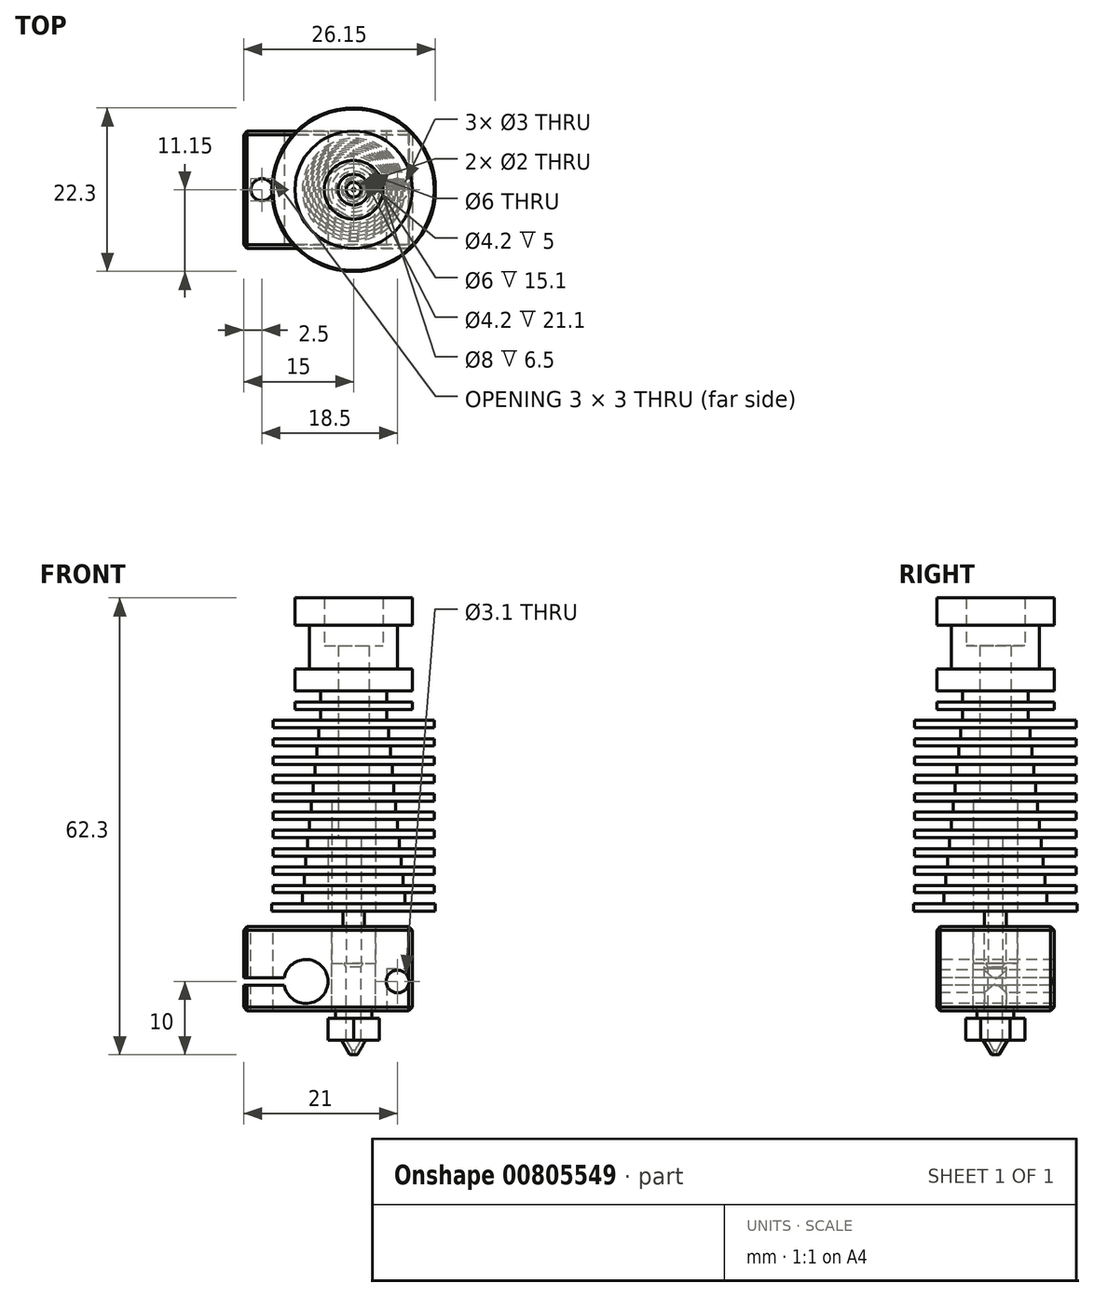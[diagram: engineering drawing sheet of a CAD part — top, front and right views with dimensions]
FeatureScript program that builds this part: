
annotation { "Feature Type Name" : "Feature", "Feature Type Description" : "" }
export const myFeature = defineFeature(function(context is Context, id is Id, definition is map)
    precondition{}
    {
        {
            var Q0;
            Q0=qCreatedBy(makeId("Front.planeOp"),FACE);
            var sketch = newSketch(context, id + "F0", { "sketchPlane" : qUnion([Q0])});
            skLineSegment(sketch, "E0", {"start": v(0, 0) * mm, "end": v(0, 45.21) * mm, "construction": true});
            skLineSegment(sketch, "E1", {"start": v(-3, 0) * mm, "end": v(-3, 15.1) * mm});
            skLineSegment(sketch, "E2", {"start": v(-3, 15.1) * mm, "end": v(-2.1, 15.1) * mm});
            skLineSegment(sketch, "E3", {"start": v(-2.1, 36.2) * mm, "end": v(-4, 36.2) * mm});
            skLineSegment(sketch, "E4", {"start": v(-4, 36.2) * mm, "end": v(-4, 42.7) * mm});
            skLineSegment(sketch, "E5", {"start": v(-4, 42.7) * mm, "end": v(-8, 42.7) * mm});
            skLineSegment(sketch, "E6", {"start": v(-8, 42.7) * mm, "end": v(-8, 39) * mm});
            skLineSegment(sketch, "E7", {"start": v(-6, 39) * mm, "end": v(-6, 33) * mm});
            skLineSegment(sketch, "E8", {"start": v(-6, 33) * mm, "end": v(-8, 33) * mm});
            skLineSegment(sketch, "E9", {"start": v(-8, 33) * mm, "end": v(-8, 30) * mm});
            skLineSegment(sketch, "E10", {"start": v(-8, 30) * mm, "end": v(-4.5, 30) * mm});
            skLineSegment(sketch, "E11", {"start": v(-4.5, 28.5) * mm, "end": v(-8, 28.5) * mm});
            skLineSegment(sketch, "E12", {"start": v(-8, 28.5) * mm, "end": v(-8, 27.5) * mm});
            skLineSegment(sketch, "E13", {"start": v(-8, 27.5) * mm, "end": v(-4.5, 27.5) * mm});
            skLineSegment(sketch, "E14", {"start": v(-4.5, 30) * mm, "end": v(-4.5, 28.5) * mm});
            skLineSegment(sketch, "E15", {"start": v(-8, 39) * mm, "end": v(-6, 39) * mm});
            skLineSegment(sketch, "E16", {"start": v(-2.1, 15.1) * mm, "end": v(-2.1, 36.2) * mm});
            skLineSegment(sketch, "E17", {"start": v(-11.15, 1) * mm, "end": v(-7, 1) * mm});
            skLineSegment(sketch, "E18", {"start": v(-7, 1) * mm, "end": v(-7, 2.5) * mm});
            skLineSegment(sketch, "E19", {"start": v(-7, 2.5) * mm, "end": v(-11, 2.5) * mm});
            skLineSegment(sketch, "E20", {"start": v(-11, 2.5) * mm, "end": v(-11, 3.5) * mm});
            skLineSegment(sketch, "E21", {"start": v(-11, 3.5) * mm, "end": v(-6.75, 3.5) * mm});
            skLineSegment(sketch, "E22", {"start": v(-6.75, 3.5) * mm, "end": v(-6.75, 5) * mm});
            skLineSegment(sketch, "E23", {"start": v(-6.75, 5) * mm, "end": v(-11, 5) * mm});
            skLineSegment(sketch, "E24", {"start": v(-11, 5) * mm, "end": v(-11, 6) * mm});
            skLineSegment(sketch, "E25", {"start": v(-11, 6) * mm, "end": v(-6.5, 6) * mm});
            skLineSegment(sketch, "E26", {"start": v(-6.5, 6) * mm, "end": v(-6.5, 7.5) * mm});
            skLineSegment(sketch, "E27", {"start": v(-6.5, 7.5) * mm, "end": v(-11, 7.5) * mm});
            skLineSegment(sketch, "E28", {"start": v(-11, 7.5) * mm, "end": v(-11, 8.5) * mm});
            skLineSegment(sketch, "E29", {"start": v(-11, 8.5) * mm, "end": v(-6.25, 8.5) * mm});
            skLineSegment(sketch, "E30", {"start": v(-6.25, 8.5) * mm, "end": v(-6.25, 10) * mm});
            skLineSegment(sketch, "E31", {"start": v(-6.25, 10) * mm, "end": v(-11, 10) * mm});
            skLineSegment(sketch, "E32", {"start": v(-11, 10) * mm, "end": v(-11, 11) * mm});
            skLineSegment(sketch, "E33", {"start": v(-11, 11) * mm, "end": v(-6, 11) * mm});
            skLineSegment(sketch, "E34", {"start": v(-6, 11) * mm, "end": v(-6, 12.5) * mm});
            skLineSegment(sketch, "E35", {"start": v(-6, 12.5) * mm, "end": v(-11, 12.5) * mm});
            skLineSegment(sketch, "E36", {"start": v(-11, 12.5) * mm, "end": v(-11, 13.5) * mm});
            skLineSegment(sketch, "E37", {"start": v(-11, 13.5) * mm, "end": v(-5.75, 13.5) * mm});
            skLineSegment(sketch, "E38", {"start": v(-5.75, 13.5) * mm, "end": v(-5.75, 15) * mm});
            skLineSegment(sketch, "E39", {"start": v(-5.75, 15) * mm, "end": v(-11, 15) * mm});
            skLineSegment(sketch, "E40", {"start": v(-11, 15) * mm, "end": v(-11, 16) * mm});
            skLineSegment(sketch, "E41", {"start": v(-11, 16) * mm, "end": v(-5.5, 16) * mm});
            skLineSegment(sketch, "E42", {"start": v(-5.5, 16) * mm, "end": v(-5.5, 17.5) * mm});
            skLineSegment(sketch, "E43", {"start": v(-5.5, 17.5) * mm, "end": v(-11, 17.5) * mm});
            skLineSegment(sketch, "E44", {"start": v(-11, 17.5) * mm, "end": v(-11, 18.5) * mm});
            skLineSegment(sketch, "E45", {"start": v(-11, 18.5) * mm, "end": v(-5.25, 18.5) * mm});
            skLineSegment(sketch, "E46", {"start": v(-5.25, 18.5) * mm, "end": v(-5.25, 20) * mm});
            skLineSegment(sketch, "E47", {"start": v(-5.25, 20) * mm, "end": v(-11, 20) * mm});
            skLineSegment(sketch, "E48", {"start": v(-11, 20) * mm, "end": v(-11, 21) * mm});
            skLineSegment(sketch, "E49", {"start": v(-11, 21) * mm, "end": v(-5, 21) * mm});
            skLineSegment(sketch, "E50", {"start": v(-5, 21) * mm, "end": v(-5, 22.5) * mm});
            skLineSegment(sketch, "E51", {"start": v(-5, 22.5) * mm, "end": v(-11, 22.5) * mm});
            skLineSegment(sketch, "E52", {"start": v(-11, 22.5) * mm, "end": v(-11, 23.5) * mm});
            skLineSegment(sketch, "E53", {"start": v(-11, 23.5) * mm, "end": v(-4.75, 23.5) * mm});
            skLineSegment(sketch, "E54", {"start": v(-4.75, 23.5) * mm, "end": v(-4.75, 25) * mm});
            skLineSegment(sketch, "E55", {"start": v(-4.75, 25) * mm, "end": v(-11, 25) * mm});
            skLineSegment(sketch, "E56", {"start": v(-11, 25) * mm, "end": v(-11, 26) * mm});
            skLineSegment(sketch, "E57", {"start": v(-11, 26) * mm, "end": v(-4.5, 26) * mm});
            skLineSegment(sketch, "E58", {"start": v(-4.5, 26) * mm, "end": v(-4.5, 27.5) * mm});
            skLineSegment(sketch, "E59", {"start": v(-3, 0) * mm, "end": v(-11.15, 0) * mm});
            skLineSegment(sketch, "E60", {"start": v(-11.15, 0) * mm, "end": v(-11.15, 1) * mm});
            skSolve(sketch);
        }
        {
            var Q0;
            Q0=qSketchRegion(id+"F0",true);
            var Q1;
            Q1=sQuery(id+"F0.wireOp",EDGE,"E0");
            revolve(context, id + "F1", {"surfaceOperationType" : NewSurfaceOperationType.NEW, "entities" : qUnion([Q0]), "axis" : qUnion([Q1]), "revolveType" : RevolveType.FULL});
        }
        {
            var Q0;
            Q0=qCreatedBy(makeId("Front.planeOp"),FACE);
            var sketch = newSketch(context, id + "F2", { "sketchPlane" : qUnion([Q0])});
            skLineSegment(sketch, "E61", {"start": v(0, 0) * mm, "end": v(0, 46.31) * mm, "construction": true});
            skLineSegment(sketch, "E62", {"start": v(-3, 15) * mm, "end": v(-3, 10) * mm});
            skLineSegment(sketch, "E63", {"start": v(-3, 10) * mm, "end": v(-3.5, 10) * mm});
            skLineSegment(sketch, "E64", {"start": v(-3.5, 10) * mm, "end": v(-3.5, 0) * mm});
            skLineSegment(sketch, "E65", {"start": v(-3.5, 0) * mm, "end": v(-1.48, 0) * mm});
            skLineSegment(sketch, "E66", {"start": v(-1.48, 0) * mm, "end": v(-1.48, -2.1) * mm});
            skLineSegment(sketch, "E67", {"start": v(-1.48, -2.1) * mm, "end": v(-3, -2.1) * mm});
            skLineSegment(sketch, "E68", {"start": v(-3, -2.1) * mm, "end": v(-3, -7.1) * mm});
            skLineSegment(sketch, "E69", {"start": v(-3, -7.1) * mm, "end": v(-1, -7.1) * mm});
            skLineSegment(sketch, "E70", {"start": v(-1, -7.1) * mm, "end": v(-1, 10) * mm});
            skLineSegment(sketch, "E71", {"start": v(-1, 10) * mm, "end": v(-2.1, 10) * mm});
            skLineSegment(sketch, "E72", {"start": v(-2.1, 10) * mm, "end": v(-2.1, 15) * mm});
            skLineSegment(sketch, "E73", {"start": v(-2.1, 15) * mm, "end": v(-3, 15) * mm});
            skSolve(sketch);
        }
        {
            var Q0;
            Q0=qSketchRegion(id+"F2",true);
            var Q1;
            Q1=sQuery(id+"F2.wireOp",EDGE,"E61");
            revolve(context, id + "F3", {"surfaceOperationType" : NewSurfaceOperationType.NEW, "entities" : qUnion([Q0]), "axis" : qUnion([Q1]), "revolveType" : RevolveType.FULL});
        }
        {
            var Q0;
            Q0=makeQuery(id+"F3.opRevolve","SWEPT_FACE",FACE,{"disambiguationData":[OSD([sQuery(id+"F2.wireOp",EDGE,"E67")])]});
            var sketch = newSketch(context, id + "F4", { "sketchPlane" : qUnion([Q0])});
            skLineSegment(sketch, "E74.bottom", {"start": v(8, -8) * mm, "end": v(-15, -8) * mm});
            skLineSegment(sketch, "E74.top", {"start": v(8, 8) * mm, "end": v(-15, 8) * mm});
            skLineSegment(sketch, "E74.left", {"start": v(8, -8) * mm, "end": v(8, 8) * mm});
            skLineSegment(sketch, "E74.right", {"start": v(-15, -8) * mm, "end": v(-15, 8) * mm});
            skLineSegment(sketch, "E75", {"start": v(-16.95, 0) * mm, "end": v(14.7, 0) * mm, "construction": true});
            skCircle(sketch, "E76", {"center": v(0, 0) * mm, "radius": 3 * mm});
            skCircle(sketch, "E77", {"center": v(6, 0) * mm, "radius": 1.5 * mm});
            skCircle(sketch, "E78", {"center": v(-12.5, 0) * mm, "radius": 1.5 * mm});
            skSolve(sketch);
        }
        {
            var Q0;
            Q0=qSketchRegion(id+"F4",true);
            var Q1;
            Q1=makeQuery(id+"F4.imprint","IMPRINT",FACE,{"disambiguationData":[TD([[makeQuery(id+"F4.imprint","IMPRINT",EDGE,{"derivedFrom":sQuery(id+"F4.wireOp",EDGE,"E77")}),1.0]])]});
            extrude(context, id + "F5", {"entities" : qUnion([Q0, Q1]), "oppositeDirection" : true, "depth" : 11.5 * mm, "offsetDistance" : 25 * mm});
        }
        {
            var Q0;
            Q0=makeQuery(id+"F5.opExtrude","CAP_FACE",FACE,{"disambiguationData":[OSD([sQuery(id+"F4.wireOp",EDGE,"E74.bottom"),sQuery(id+"F4.wireOp",EDGE,"E74.top"),sQuery(id+"F4.wireOp",EDGE,"E74.left"),sQuery(id+"F4.wireOp",EDGE,"E74.right"),sQuery(id+"F4.wireOp",EDGE,"E76"),sQuery(id+"F4.wireOp",EDGE,"E78")])],"isStart":false});
            var sketch = newSketch(context, id + "F6", { "sketchPlane" : qUnion([Q0])});
            skCircle(sketch, "E79.0", {"center": v(6, 0) * mm, "radius": 1.5 * mm});
            skSolve(sketch);
        }
        {
            var Q0;
            Q0=qSketchRegion(id+"F6",true);
            extrude(context, id + "F7", {"entities" : qUnion([Q0]), "operationType" : NewBodyOperationType.REMOVE, "oppositeDirection" : true, "depth" : 5.75 * mm, "offsetDistance" : 25 * mm});
        }
        {
            var Q0;
            Q0=makeQuery(id+"F5.opExtrude","SWEPT_FACE",FACE,{"disambiguationData":[OSD([sQuery(id+"F4.wireOp",EDGE,"E74.bottom")])]});
            var sketch = newSketch(context, id + "F8", { "sketchPlane" : qUnion([Q0])});
            skLineSegment(sketch, "E80", {"start": v(-15.75, -9.6) * mm, "end": v(10.37, -9.6) * mm, "construction": true});
            skCircle(sketch, "E81", {"center": v(-6.5, -9.6) * mm, "radius": 3 * mm});
            skCircle(sketch, "E82", {"center": v(6, -9.6) * mm, "radius": 1.55 * mm});
            skLineSegment(sketch, "E83", {"start": v(-15, -10.1) * mm, "end": v(-9.46, -10.1) * mm});
            skPoint(sketch, "E84.startSnap0", {"position": v(-15, -7.85) * mm});
            skLineSegment(sketch, "E85", {"start": v(-15, -10.1) * mm, "end": v(-15, -9.1) * mm});
            skLineSegment(sketch, "E86", {"start": v(-15, -9.1) * mm, "end": v(-9.46, -9.1) * mm});
            skSolve(sketch);
        }
        {
            var Q0;
            Q0=qSketchRegion(id+"F8",true);
            var Q1;
            Q1=makeQuery(id+"F5.opExtrude","SWEPT_FACE",FACE,{"disambiguationData":[OSD([sQuery(id+"F4.wireOp",EDGE,"E74.top")])]});
            extrude(context, id + "F9", {"entities" : qUnion([Q0]), "operationType" : NewBodyOperationType.REMOVE, "endBound" : BoundingType.UP_TO_SURFACE, "oppositeDirection" : true, "depth" : 25 * mm, "endBoundEntityFace" : qUnion([Q1]), "offsetDistance" : 25 * mm});
        }
        {
            var Q0;
            Q0=makeQuery(id+"F5.opExtrude","CAP_EDGE",EDGE,{"disambiguationData":[OSD([sQuery(id+"F4.wireOp",EDGE,"E74.bottom")])],"isStart":true});
            var Q1;
            Q1=makeQuery(id+"F5.opExtrude","CAP_EDGE",EDGE,{"disambiguationData":[OSD([sQuery(id+"F4.wireOp",EDGE,"E74.right")])],"isStart":true});
            var Q2;
            {var subQ0=sQuery(id+"F4.wireOp",EDGE,"E74.bottom");var subQ1=sQuery(id+"F4.wireOp",EDGE,"E74.right");Q2=makeQuery(id+"F9.boolean.opBoolean","SPLIT",EDGE,{"disambiguationData":[TD([makeQuery(id+"F9.opExtrude","SWEPT_FACE",FACE,{"disambiguationData":[OSD([sQuery(id+"F8.wireOp",EDGE,"E86")])]})])],"derivedFrom":makeQuery(id+"F5.opExtrude","SWEPT_EDGE",EDGE,{"disambiguationData":[OSD([subQ0,subQ1])]})});}
            var Q3;
            {var subQ0=sQuery(id+"F4.wireOp",EDGE,"E74.bottom");var subQ1=sQuery(id+"F4.wireOp",EDGE,"E74.right");Q3=makeQuery(id+"F9.boolean.opBoolean","SPLIT",EDGE,{"disambiguationData":[TD([makeQuery(id+"F9.opExtrude","SWEPT_FACE",FACE,{"disambiguationData":[OSD([sQuery(id+"F8.wireOp",EDGE,"E83")])]})])],"derivedFrom":makeQuery(id+"F5.opExtrude","SWEPT_EDGE",EDGE,{"disambiguationData":[OSD([subQ0,subQ1])]})});}
            var Q4;
            Q4=makeQuery(id+"F5.opExtrude","SWEPT_EDGE",EDGE,{"disambiguationData":[OSD([sQuery(id+"F4.wireOp",EDGE,"E74.bottom"),sQuery(id+"F4.wireOp",EDGE,"E74.left")])]});
            var Q5;
            Q5=makeQuery(id+"F5.opExtrude","CAP_EDGE",EDGE,{"disambiguationData":[OSD([sQuery(id+"F4.wireOp",EDGE,"E74.bottom")])],"isStart":false});
            var Q6;
            Q6=makeQuery(id+"F5.opExtrude","CAP_EDGE",EDGE,{"disambiguationData":[OSD([sQuery(id+"F4.wireOp",EDGE,"E74.right")])],"isStart":false});
            var Q7;
            Q7=makeQuery(id+"F5.opExtrude","CAP_EDGE",EDGE,{"disambiguationData":[OSD([sQuery(id+"F4.wireOp",EDGE,"E74.left")])],"isStart":false});
            var Q8;
            Q8=makeQuery(id+"F5.opExtrude","CAP_EDGE",EDGE,{"disambiguationData":[OSD([sQuery(id+"F4.wireOp",EDGE,"E74.left")])],"isStart":true});
            var Q9;
            Q9=makeQuery(id+"F5.opExtrude","SWEPT_EDGE",EDGE,{"disambiguationData":[OSD([sQuery(id+"F4.wireOp",EDGE,"E74.top"),sQuery(id+"F4.wireOp",EDGE,"E74.left")])]});
            var Q10;
            Q10=makeQuery(id+"F5.opExtrude","CAP_EDGE",EDGE,{"disambiguationData":[OSD([sQuery(id+"F4.wireOp",EDGE,"E74.top")])],"isStart":true});
            var Q11;
            Q11=makeQuery(id+"F5.opExtrude","CAP_EDGE",EDGE,{"disambiguationData":[OSD([sQuery(id+"F4.wireOp",EDGE,"E74.top")])],"isStart":false});
            var Q12;
            {var subQ0=sQuery(id+"F4.wireOp",EDGE,"E74.right");var subQ1=sQuery(id+"F4.wireOp",EDGE,"E74.top");Q12=makeQuery(id+"F9.boolean.opBoolean","SPLIT",EDGE,{"disambiguationData":[TD([makeQuery(id+"F9.opExtrude","SWEPT_FACE",FACE,{"disambiguationData":[OSD([sQuery(id+"F8.wireOp",EDGE,"E83")])]})])],"derivedFrom":makeQuery(id+"F5.opExtrude","SWEPT_EDGE",EDGE,{"disambiguationData":[OSD([subQ1,subQ0])]})});}
            var Q13;
            {var subQ0=sQuery(id+"F4.wireOp",EDGE,"E74.right");var subQ1=sQuery(id+"F4.wireOp",EDGE,"E74.top");Q13=makeQuery(id+"F9.boolean.opBoolean","SPLIT",EDGE,{"disambiguationData":[TD([makeQuery(id+"F9.opExtrude","SWEPT_FACE",FACE,{"disambiguationData":[OSD([sQuery(id+"F8.wireOp",EDGE,"E86")])]})])],"derivedFrom":makeQuery(id+"F5.opExtrude","SWEPT_EDGE",EDGE,{"disambiguationData":[OSD([subQ1,subQ0])]})});}
            chamfer(context, id + "F10", {"entities" : qUnion([Q0, Q1, Q2, Q3, Q4, Q5, Q6, Q7, Q8, Q9, Q10, Q11, Q12, Q13]), "width" : .5 * mm, "tangentPropagation" : true});
        }
        {
            var Q0;
            Q0=qCreatedBy(makeId("Front.planeOp"),FACE);
            var sketch = newSketch(context, id + "F11", { "sketchPlane" : qUnion([Q0])});
            skLineSegment(sketch, "E87", {"start": v(0, 0) * mm, "end": v(0, -17.7) * mm, "construction": true});
            skLineSegment(sketch, "E88", {"start": v(-1.3, -7.1) * mm, "end": v(-3, -7.1) * mm});
            skLineSegment(sketch, "E89", {"start": v(-3, -7.1) * mm, "end": v(-3, -13.1) * mm});
            skLineSegment(sketch, "E90", {"start": v(-3, -13.1) * mm, "end": v(-2.5, -13.1) * mm});
            skLineSegment(sketch, "E91", {"start": v(-2.5, -13.1) * mm, "end": v(-2.5, -14.6) * mm});
            skLineSegment(sketch, "E92", {"start": v(-2.5, -14.6) * mm, "end": v(-6, -14.6) * mm});
            skLineSegment(sketch, "E93", {"start": v(-6, -14.6) * mm, "end": v(-6, -17.6) * mm});
            skLineSegment(sketch, "E94", {"start": v(-6, -17.6) * mm, "end": v(-1.65, -17.6) * mm});
            skLineSegment(sketch, "E95", {"start": v(-1.65, -17.6) * mm, "end": v(-0.5, -19.6) * mm});
            skLineSegment(sketch, "E96", {"start": v(-0.5, -19.6) * mm, "end": v(-0.2, -19.6) * mm});
            skLineSegment(sketch, "E97", {"start": v(-0.2, -19.6) * mm, "end": v(-0.2, -19) * mm});
            skLineSegment(sketch, "E98", {"start": v(-0.2, -19) * mm, "end": v(-1, -17.61) * mm});
            skLineSegment(sketch, "E99", {"start": v(-1, -17.61) * mm, "end": v(-1, -7.62) * mm});
            skLineSegment(sketch, "E100", {"start": v(-1, -7.62) * mm, "end": v(-1.3, -7.1) * mm});
            skSolve(sketch);
        }
        {
            var Q0;
            Q0=qSketchRegion(id+"F11",true);
            var Q1;
            Q1=sQuery(id+"F11.wireOp",EDGE,"E87");
            revolve(context, id + "F12", {"surfaceOperationType" : NewSurfaceOperationType.NEW, "entities" : qUnion([Q0]), "axis" : qUnion([Q1]), "revolveType" : RevolveType.FULL});
        }
        {
            var Q0;
            Q0=makeQuery(id+"F12.opRevolve","SWEPT_FACE",FACE,{"disambiguationData":[OSD([sQuery(id+"F11.wireOp",EDGE,"E94")])]});
            var sketch = newSketch(context, id + "F13", { "sketchPlane" : qUnion([Q0])});
            skCircle(sketch, "E101.cCircle", {"center": v(0, 0) * mm, "radius": 3.5 * mm, "construction": true});
            skLineSegment(sketch, "E101.0", {"start": v(3.5, -2.02) * mm, "end": v(0, -4.04) * mm});
            skLineSegment(sketch, "E101.1", {"start": v(0, -4.04) * mm, "end": v(-3.5, -2.02) * mm});
            skLineSegment(sketch, "E101.2", {"start": v(-3.5, -2.02) * mm, "end": v(-3.5, 2.02) * mm});
            skLineSegment(sketch, "E101.3", {"start": v(-3.5, 2.02) * mm, "end": v(0, 4.04) * mm});
            skLineSegment(sketch, "E101.4", {"start": v(0, 4.04) * mm, "end": v(3.5, 2.02) * mm});
            skLineSegment(sketch, "E101.5", {"start": v(3.5, 2.02) * mm, "end": v(3.5, -2.02) * mm});
            skPoint(sketch, "E101.0.midPoint", {"position": v(1.75, -3.03) * mm});
            skLineSegment(sketch, "E102", {"start": v(0, 0) * mm, "end": v(0, 18.08) * mm, "construction": true});
            skCircle(sketch, "E103", {"center": v(0, 0) * mm, "radius": 6.55 * mm});
            skSolve(sketch);
        }
        {
            var Q0;
            Q0=qSketchRegion(id+"F13",true);
            var Q1;
            Q1=makeQuery(id+"F12.opRevolve","SWEPT_FACE",FACE,{"disambiguationData":[OSD([sQuery(id+"F11.wireOp",EDGE,"E92")])]});
            extrude(context, id + "F14", {"entities" : qUnion([Q0]), "operationType" : NewBodyOperationType.REMOVE, "endBound" : BoundingType.UP_TO_SURFACE, "oppositeDirection" : true, "depth" : 25 * mm, "endBoundEntityFace" : qUnion([Q1]), "offsetDistance" : 25 * mm});
        }
        {
            var Q0;
            Q0=makeQuery(id+"F12.opRevolve","SWEPT_EDGE",EDGE,{"disambiguationData":[OSD([sQuery(id+"F11.wireOp",EDGE,"E95"),sQuery(id+"F11.wireOp",EDGE,"E96")])]});
            fillet(context, id + "F15", {"entities" : qUnion([Q0]), "radius" : .2 * mm, "tangentPropagation" : true, "allowEdgeOverflow" : false});
        }
    });
